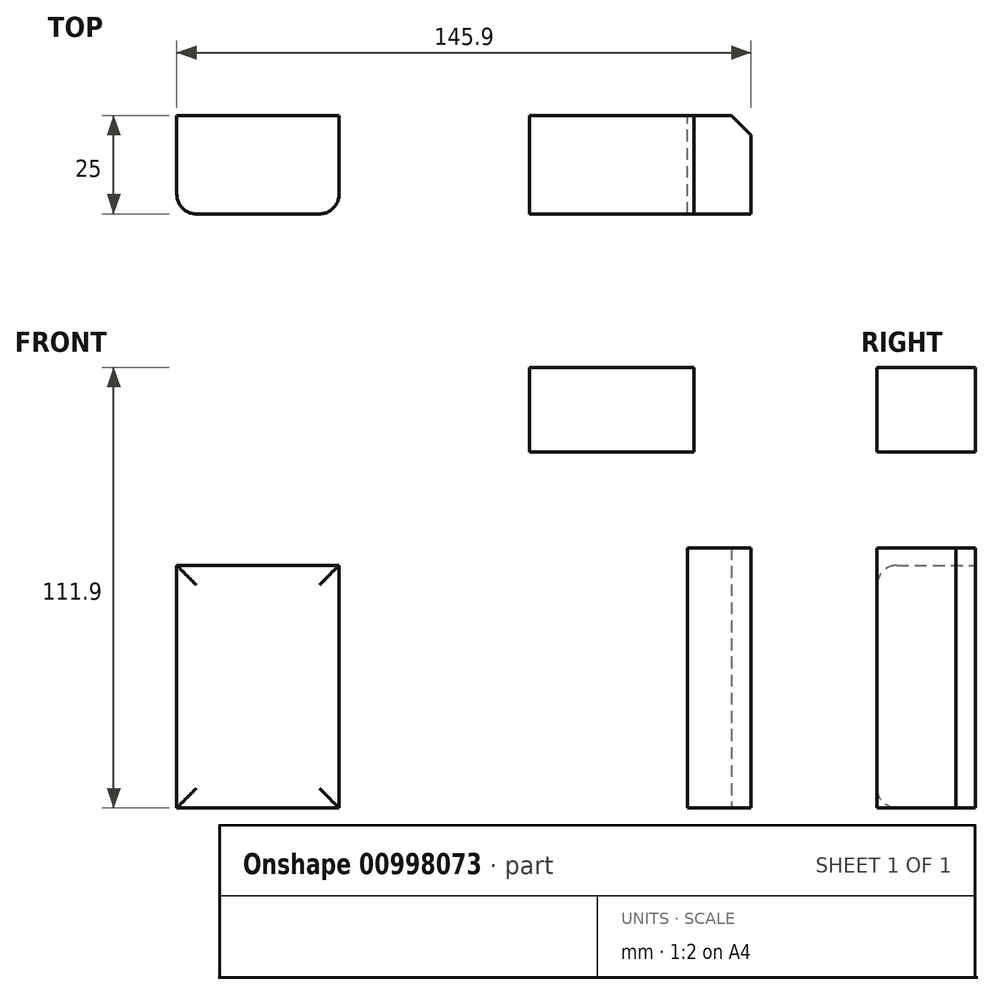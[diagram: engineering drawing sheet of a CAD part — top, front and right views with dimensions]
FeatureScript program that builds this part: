
annotation { "Feature Type Name" : "Feature", "Feature Type Description" : "" }
export const myFeature = defineFeature(function(context is Context, id is Id, definition is map)
    precondition{}
    {
        {
            var Q0;
            Q0=qCreatedBy(makeId("Front.planeOp"),FACE);
            var sketch = newSketch(context, id + "F0", { "sketchPlane" : qUnion([Q0])});
            skLineSegment(sketch, "E0.bottom", {"start": v(-66.02, 61.6) * mm, "end": v(-24.8, 61.6) * mm});
            skLineSegment(sketch, "E0.top", {"start": v(-66.02, 0) * mm, "end": v(-24.8, 0) * mm});
            skLineSegment(sketch, "E0.left", {"start": v(-66.02, 61.6) * mm, "end": v(-66.02, 0) * mm});
            skLineSegment(sketch, "E0.right", {"start": v(-24.8, 61.6) * mm, "end": v(-24.8, 0) * mm});
            skLineSegment(sketch, "E1.bottom", {"start": v(63.67, 66.04) * mm, "end": v(79.88, 66.04) * mm});
            skLineSegment(sketch, "E1.top", {"start": v(63.67, 0) * mm, "end": v(79.88, 0) * mm});
            skLineSegment(sketch, "E1.left", {"start": v(63.67, 66.04) * mm, "end": v(63.67, 0) * mm});
            skLineSegment(sketch, "E1.right", {"start": v(79.88, 66.04) * mm, "end": v(79.88, 0) * mm});
            skLineSegment(sketch, "E2.bottom", {"start": v(-45.9, -78.48) * mm, "end": v(18.55, -78.48) * mm});
            skLineSegment(sketch, "E2.top", {"start": v(-45.9, -82.92) * mm, "end": v(18.55, -82.92) * mm});
            skLineSegment(sketch, "E2.left", {"start": v(-45.9, -78.48) * mm, "end": v(-45.9, -82.92) * mm});
            skLineSegment(sketch, "E2.right", {"start": v(18.55, -78.48) * mm, "end": v(18.55, -82.92) * mm});
            skLineSegment(sketch, "E3.bottom", {"start": v(23.63, 111.9) * mm, "end": v(65.43, 111.9) * mm});
            skLineSegment(sketch, "E3.top", {"start": v(23.63, 90.37) * mm, "end": v(65.43, 90.37) * mm});
            skLineSegment(sketch, "E3.left", {"start": v(23.63, 111.9) * mm, "end": v(23.63, 90.37) * mm});
            skLineSegment(sketch, "E3.right", {"start": v(65.43, 111.9) * mm, "end": v(65.43, 90.37) * mm});
            skSolve(sketch);
        }
        {
            var Q0;
            Q0=makeQuery(id+"F0.imprint","IMPRINT",FACE,{"disambiguationData":[TD([[makeQuery(id+"F0.imprint","IMPRINT",EDGE,{"derivedFrom":sQuery(id+"F0.wireOp",EDGE,"E0.bottom")}),-1.0]])]});
            extrude(context, id + "F1", {"entities" : qUnion([Q0]), "depth" : 25 * mm, "offsetDistance" : 25 * mm});
        }
        {
            var Q0;
            Q0=makeQuery(id+"F0.imprint","IMPRINT",FACE,{"disambiguationData":[TD([[makeQuery(id+"F0.imprint","IMPRINT",EDGE,{"derivedFrom":sQuery(id+"F0.wireOp",EDGE,"E1.bottom")}),-1.0]])]});
            extrude(context, id + "F2", {"entities" : qUnion([Q0]), "depth" : 25 * mm, "offsetDistance" : 25 * mm});
        }
        {
            var Q0;
            Q0=makeQuery(id+"F0.imprint","IMPRINT",FACE,{"disambiguationData":[TD([[makeQuery(id+"F0.imprint","IMPRINT",EDGE,{"derivedFrom":sQuery(id+"F0.wireOp",EDGE,"E3.bottom")}),-1.0]])]});
            extrude(context, id + "F3", {"entities" : qUnion([Q0]), "depth" : 25 * mm, "offsetDistance" : 25 * mm});
        }
        {
            var Q0;
            Q0=makeQuery(id+"F1.opExtrude","CAP_FACE",FACE,{"disambiguationData":[OSD([sQuery(id+"F0.wireOp",EDGE,"E0.bottom"),sQuery(id+"F0.wireOp",EDGE,"E0.top"),sQuery(id+"F0.wireOp",EDGE,"E0.left"),sQuery(id+"F0.wireOp",EDGE,"E0.right")])],"isStart":false});
            fillet(context, id + "F4", {"entities" : qUnion([Q0]), "radius" : 5 * mm, "tangentPropagation" : true, "allowEdgeOverflow" : false});
        }
        {
            var Q0;
            Q0=makeQuery(id+"F2.opExtrude","CAP_EDGE",EDGE,{"disambiguationData":[OSD([sQuery(id+"F0.wireOp",EDGE,"E1.right")])],"isStart":true});
            chamfer(context, id + "F5", {"entities" : qUnion([Q0]), "width" : 5 * mm, "tangentPropagation" : true});
        }
    });
